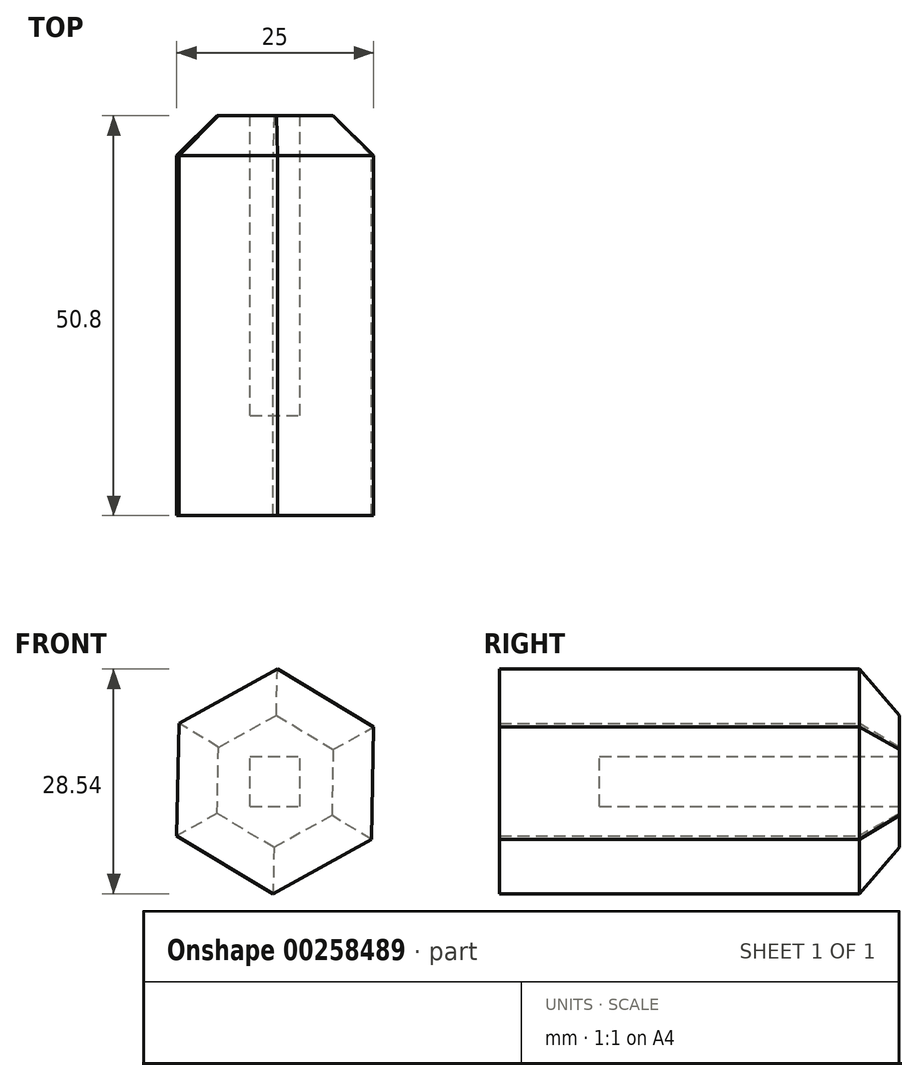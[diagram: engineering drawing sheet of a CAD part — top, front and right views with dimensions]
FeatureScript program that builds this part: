
annotation { "Feature Type Name" : "Feature", "Feature Type Description" : "" }
export const myFeature = defineFeature(function(context is Context, id is Id, definition is map)
    precondition{}
    {
        {
            var Q0;
            Q0=qCreatedBy(makeId("Front.planeOp"),FACE);
            var sketch = newSketch(context, id + "F0", { "sketchPlane" : qUnion([Q0])});
            skCircle(sketch, "E0.cCircle", {"center": v(0, 0) * mm, "radius": 12.36 * mm, "construction": true});
            skLineSegment(sketch, "E0.0", {"start": v(0.27, 14.27) * mm, "end": v(12.5, 6.9) * mm});
            skLineSegment(sketch, "E0.1", {"start": v(12.5, 6.9) * mm, "end": v(12.22, -7.37) * mm});
            skLineSegment(sketch, "E0.2", {"start": v(12.22, -7.37) * mm, "end": v(-0.27, -14.27) * mm});
            skLineSegment(sketch, "E0.3", {"start": v(-0.27, -14.27) * mm, "end": v(-12.5, -6.9) * mm});
            skLineSegment(sketch, "E0.4", {"start": v(-12.5, -6.9) * mm, "end": v(-12.22, 7.37) * mm});
            skLineSegment(sketch, "E0.5", {"start": v(-12.22, 7.37) * mm, "end": v(0.27, 14.27) * mm});
            skPoint(sketch, "E0.0.midPoint", {"position": v(6.39, 10.59) * mm});
            skSolve(sketch);
        }
        {
            var Q0;
            Q0=makeQuery(id+"F0.imprint","IMPRINT",FACE,{"disambiguationData":[TD([[makeQuery(id+"F0.imprint","IMPRINT",EDGE,{"derivedFrom":sQuery(id+"F0.wireOp",EDGE,"E0.0")}),-1.0]])]});
            extrude(context, id + "F1", {"entities" : qUnion([Q0]), "depth" : 50.8 * mm});
        }
        {
            var Q0;
            Q0=makeQuery(id+"F1.opExtrude","CAP_EDGE",EDGE,{"disambiguationData":[OSD([sQuery(id+"F0.wireOp",EDGE,"E0.0")])],"isStart":true});
            var Q1;
            Q1=makeQuery(id+"F1.opExtrude","CAP_EDGE",EDGE,{"disambiguationData":[OSD([sQuery(id+"F0.wireOp",EDGE,"E0.1")])],"isStart":true});
            var Q2;
            Q2=makeQuery(id+"F1.opExtrude","CAP_EDGE",EDGE,{"disambiguationData":[OSD([sQuery(id+"F0.wireOp",EDGE,"E0.2")])],"isStart":true});
            var Q3;
            Q3=makeQuery(id+"F1.opExtrude","CAP_EDGE",EDGE,{"disambiguationData":[OSD([sQuery(id+"F0.wireOp",EDGE,"E0.3")])],"isStart":true});
            var Q4;
            Q4=makeQuery(id+"F1.opExtrude","CAP_EDGE",EDGE,{"disambiguationData":[OSD([sQuery(id+"F0.wireOp",EDGE,"E0.4")])],"isStart":true});
            var Q5;
            Q5=makeQuery(id+"F1.opExtrude","CAP_EDGE",EDGE,{"disambiguationData":[OSD([sQuery(id+"F0.wireOp",EDGE,"E0.5")])],"isStart":true});
            chamfer(context, id + "F2", {"entities" : qUnion([Q0, Q1, Q2, Q3, Q4, Q5]), "width" : 5.08 * mm, "tangentPropagation" : true});
        }
        {
            var Q0;
            Q0=makeQuery(id+"F1.opExtrude","CAP_FACE",FACE,{"disambiguationData":[OSD([sQuery(id+"F0.wireOp",EDGE,"E0.0"),sQuery(id+"F0.wireOp",EDGE,"E0.1"),sQuery(id+"F0.wireOp",EDGE,"E0.2"),sQuery(id+"F0.wireOp",EDGE,"E0.3"),sQuery(id+"F0.wireOp",EDGE,"E0.4"),sQuery(id+"F0.wireOp",EDGE,"E0.5")])],"isStart":true});
            var sketch = newSketch(context, id + "F3", { "sketchPlane" : qUnion([Q0])});
            skLineSegment(sketch, "E1.bottom", {"start": v(3.18, -3.18) * mm, "end": v(-3.18, -3.18) * mm});
            skLineSegment(sketch, "E1.top", {"start": v(3.18, 3.18) * mm, "end": v(-3.18, 3.18) * mm});
            skLineSegment(sketch, "E1.left", {"start": v(3.18, -3.18) * mm, "end": v(3.18, 3.18) * mm});
            skLineSegment(sketch, "E1.right", {"start": v(-3.18, -3.18) * mm, "end": v(-3.18, 3.18) * mm});
            skPoint(sketch, "E1.middle", {"position": v(0, 0) * mm});
            skSolve(sketch);
        }
        {
            var Q0;
            Q0=makeQuery(id+"F3.imprint","IMPRINT",FACE,{"disambiguationData":[TD([[makeQuery(id+"F3.imprint","IMPRINT",EDGE,{"derivedFrom":sQuery(id+"F3.wireOp",EDGE,"E1.bottom")}),-1.0]])]});
            extrude(context, id + "F4", {"entities" : qUnion([Q0]), "operationType" : NewBodyOperationType.REMOVE, "oppositeDirection" : true, "depth" : 38.1 * mm});
        }
    });
